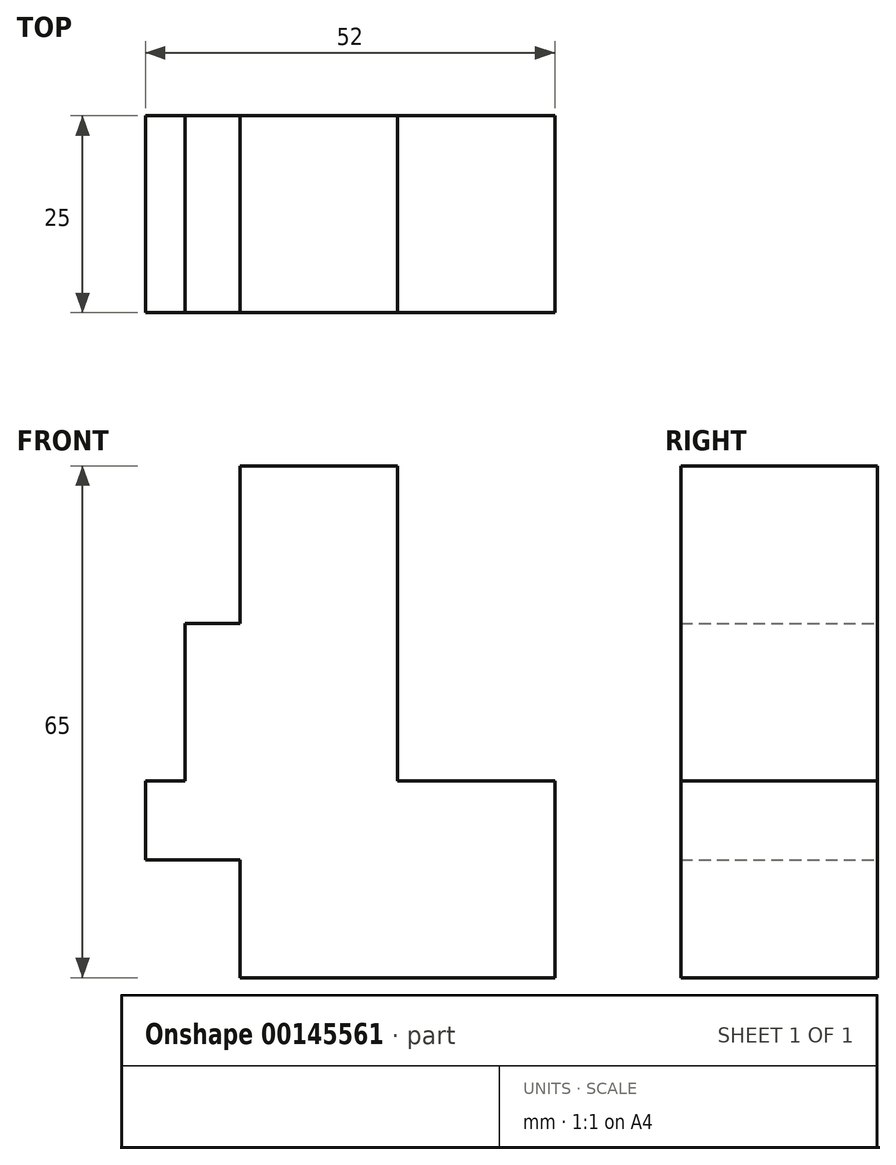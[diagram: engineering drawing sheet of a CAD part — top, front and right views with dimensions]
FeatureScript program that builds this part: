
annotation { "Feature Type Name" : "Feature", "Feature Type Description" : "" }
export const myFeature = defineFeature(function(context is Context, id is Id, definition is map)
    precondition{}
    {
        {
            var Q0;
            Q0=qCreatedBy(makeId("Front.planeOp"),FACE);
            var sketch = newSketch(context, id + "F0", { "sketchPlane" : qUnion([Q0])});
            skLineSegment(sketch, "E0.bottom", {"start": v(0, 0) * mm, "end": v(40, 0) * mm});
            skLineSegment(sketch, "E0.top", {"start": v(0, -25) * mm, "end": v(40, -25) * mm});
            skLineSegment(sketch, "E0.left", {"start": v(0, 0) * mm, "end": v(0, -25) * mm});
            skLineSegment(sketch, "E0.right", {"start": v(40, 0) * mm, "end": v(40, -25) * mm});
            skLineSegment(sketch, "E1.bottom", {"start": v(0, 0) * mm, "end": v(20, 0) * mm});
            skLineSegment(sketch, "E1.top", {"start": v(0, 40) * mm, "end": v(20, 40) * mm});
            skLineSegment(sketch, "E1.left", {"start": v(0, 0) * mm, "end": v(0, 40) * mm});
            skLineSegment(sketch, "E1.right", {"start": v(20, 0) * mm, "end": v(20, 40) * mm});
            skLineSegment(sketch, "E2.bottom", {"start": v(0, 0) * mm, "end": v(-12, 0) * mm});
            skLineSegment(sketch, "E2.top", {"start": v(0, -10) * mm, "end": v(-12, -10) * mm});
            skLineSegment(sketch, "E2.left", {"start": v(0, 0) * mm, "end": v(0, -10) * mm});
            skLineSegment(sketch, "E2.right", {"start": v(-12, 0) * mm, "end": v(-12, -10) * mm});
            skLineSegment(sketch, "E3.bottom", {"start": v(0, 0) * mm, "end": v(-7, 0) * mm});
            skLineSegment(sketch, "E3.top", {"start": v(0, 20) * mm, "end": v(-7, 20) * mm});
            skLineSegment(sketch, "E3.left", {"start": v(0, 0) * mm, "end": v(0, 20) * mm});
            skLineSegment(sketch, "E3.right", {"start": v(-7, 0) * mm, "end": v(-7, 20) * mm});
            skSolve(sketch);
        }
        {
            var Q0;
            Q0 = qSketchRegion(id + "F0", true);
            extrude(context, id + "F1", {"entities" : qUnion([Q0]), "depth" : 25 * mm});
        }
    });
